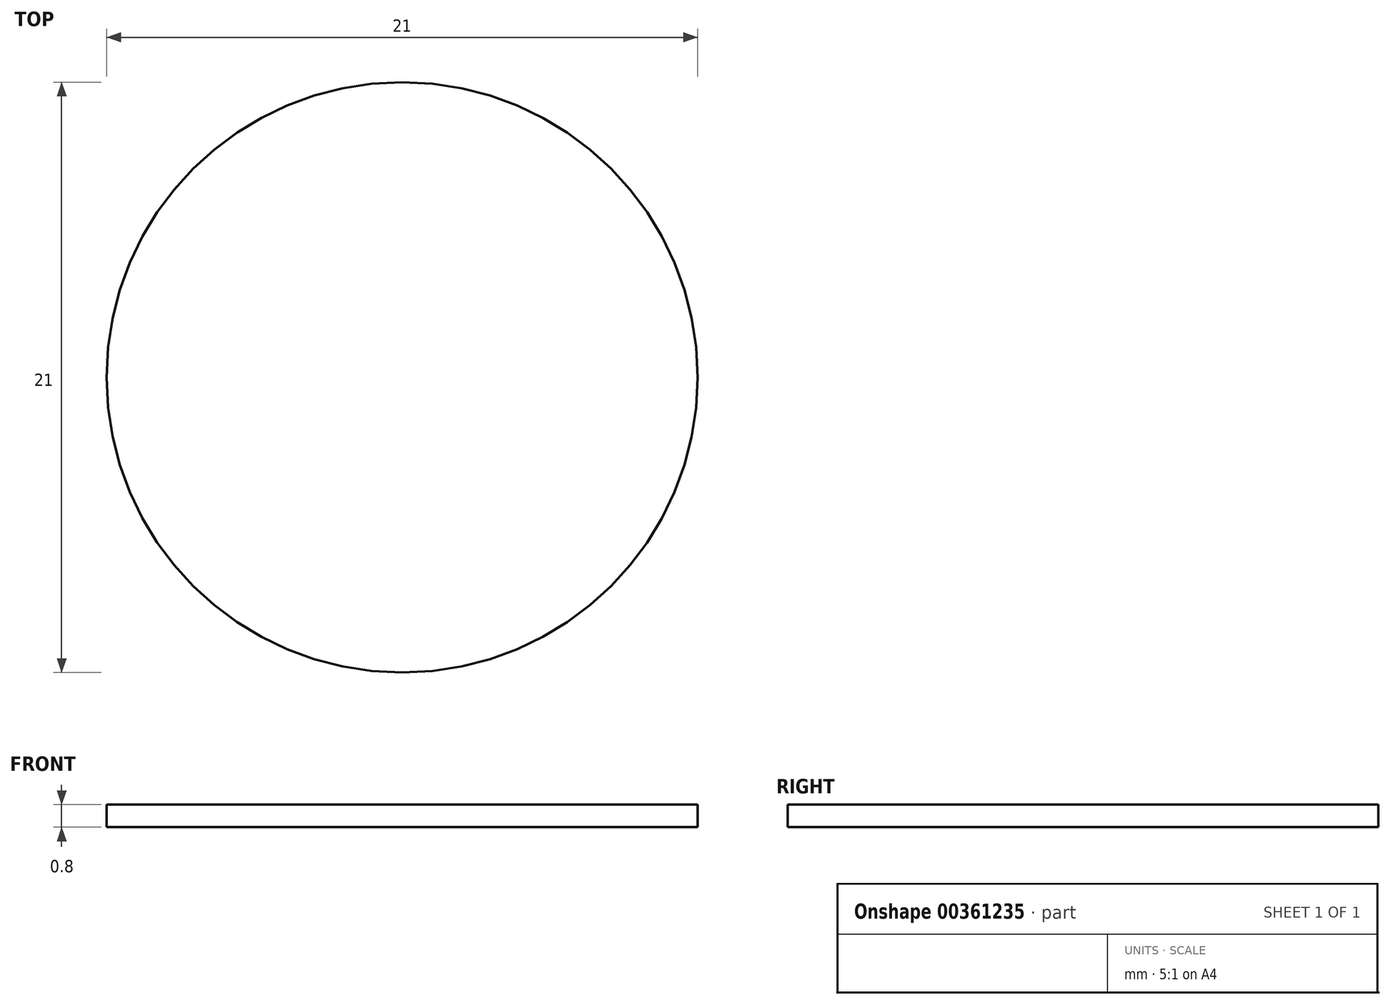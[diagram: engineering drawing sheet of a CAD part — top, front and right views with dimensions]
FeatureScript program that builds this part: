
annotation { "Feature Type Name" : "Feature", "Feature Type Description" : "" }
export const myFeature = defineFeature(function(context is Context, id is Id, definition is map)
    precondition{}
    {
        {
            var Q0;
            Q0=qCreatedBy(makeId("Top.planeOp"),FACE);
            var sketch = newSketch(context, id + "F0", { "sketchPlane" : qUnion([Q0])});
            skCircle(sketch, "E0", {"center": v(0, 0) * mm, "radius": 10.5 * mm});
            skSolve(sketch);
        }
        {
            var Q0;
            Q0=qSketchRegion(id+"F0",true);
            extrude(context, id + "F1", {"entities" : qUnion([Q0]), "depth" : 0.8 * mm, "offsetDistance" : 25 * mm});
        }
    });
